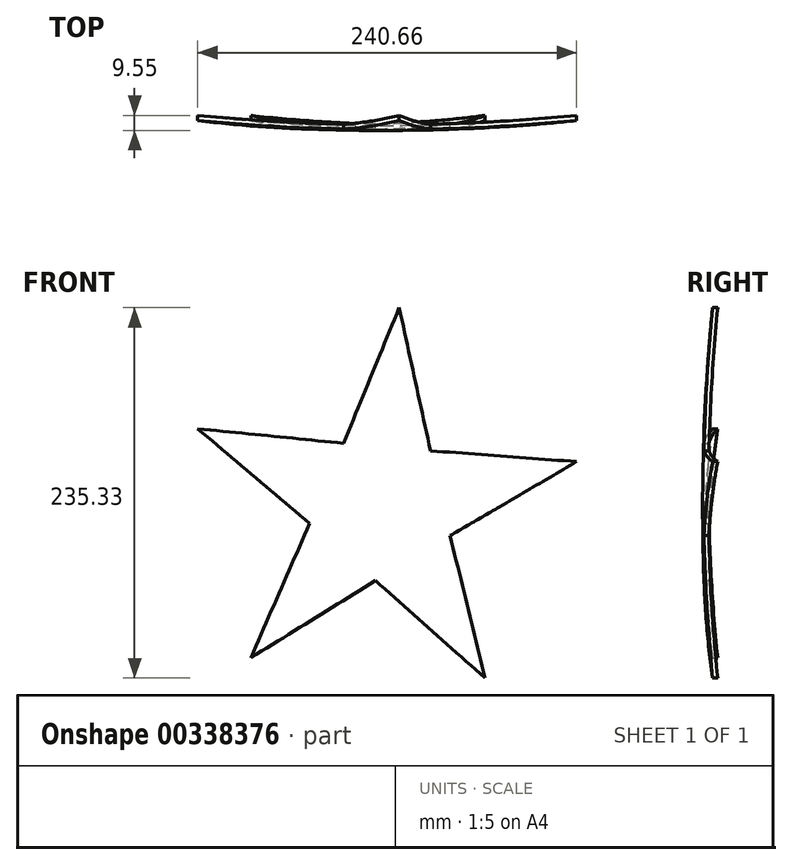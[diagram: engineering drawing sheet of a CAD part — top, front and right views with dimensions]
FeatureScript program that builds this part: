
annotation { "Feature Type Name" : "Feature", "Feature Type Description" : "" }
export const myFeature = defineFeature(function(context is Context, id is Id, definition is map)
    precondition{}
    {
        {
            var Q0;
            Q0=qCreatedBy(makeId("Top.planeOp"),FACE);
            var sketch = newSketch(context, id + "F0", { "sketchPlane" : qUnion([Q0])});
            skCircle(sketch, "E0", {"center": v(0, 986.65) * mm, "radius": 1270 * mm});
            skCircle(sketch, "E1", {"center": v(0, 986.65) * mm, "radius": 1263.65 * mm});
            skLineSegment(sketch, "E2", {"start": v(0, -277) * mm, "end": v(0, -283.35) * mm});
            skPoint(sketch, "E3", {"position": v(-508, -267.7) * mm});
            skLineSegment(sketch, "E4", {"start": v(-508, -267.7) * mm, "end": v(-508, -177.33) * mm});
            skLineSegment(sketch, "E5", {"start": v(-508, -177.33) * mm, "end": v(508, -177.33) * mm});
            skPoint(sketch, "E6", {"position": v(-177.8, -515.61) * mm});
            skPoint(sketch, "E7", {"position": v(-403.32, -498.82) * mm});
            skPoint(sketch, "E8", {"position": v(254, -269.6) * mm});
            skPoint(sketch, "E9", {"position": v(381, -241.86) * mm});
            skPoint(sketch, "E10.start.orphan", {"position": v(0, -280.18) * mm});
            skCircle(sketch, "E11", {"center": v(0, 986.65) * mm, "radius": 1266.83 * mm});
            skPoint(sketch, "E12.start.orphan", {"position": v(127, -280.18) * mm});
            skLineSegment(sketch, "E13", {"start": v(381, -241.86) * mm, "end": v(381, -221.53) * mm});
            skLineSegment(sketch, "E14", {"start": v(254, -269.6) * mm, "end": v(254, -254.45) * mm});
            skLineSegment(sketch, "E15", {"start": v(127, -280.18) * mm, "end": v(127, -273.8) * mm});
            skSolve(sketch);
        }
        {
            var Q0;
            {var subQ0=sQuery(id+"F0.wireOp",EDGE,"E2");var subQ1=sQuery(id+"F0.wireOp",EDGE,"E0");var subQ2=makeQuery(id+"F0.imprint","INTERSECT",VERTEX,{"derivedFrom":[subQ1,subQ0]});Q0=makeQuery(id+"F0.imprint","IMPRINT",FACE,{"disambiguationData":[TD([[makeQuery(id+"F0.imprint","IMPRINT",EDGE,{"disambiguationData":[TD([[subQ2,-1.0]])],"derivedFrom":subQ1}),1.0]])]});}
            var Q1;
            Q1=sQuery(id+"F0.wireOp",EDGE,"E2");
            revolve(context, id + "F1", {"entities" : qUnion([Q0]), "axis" : qUnion([Q1]), "revolveType" : RevolveType.FULL});
        }
        {
            var Q0;
            Q0=qCreatedBy(makeId("Front.planeOp"),FACE);
            var sketch = newSketch(context, id + "F2", { "sketchPlane" : qUnion([Q0])});
            skPoint(sketch, "E16", {"position": v(0, 0) * mm});
            skCircle(sketch, "E17", {"center": v(0, 0) * mm, "radius": 127 * mm});
            skCircle(sketch, "E18.cCircle", {"center": v(0, 0) * mm, "radius": 38.1 * mm, "construction": true});
            skLineSegment(sketch, "E18.0", {"start": v(-45.88, -10.63) * mm, "end": v(-24.28, 40.35) * mm});
            skLineSegment(sketch, "E18.1", {"start": v(-24.28, 40.35) * mm, "end": v(30.87, 35.56) * mm});
            skLineSegment(sketch, "E18.2", {"start": v(30.87, 35.56) * mm, "end": v(43.36, -18.37) * mm});
            skLineSegment(sketch, "E18.3", {"start": v(43.36, -18.37) * mm, "end": v(-4.07, -46.92) * mm});
            skLineSegment(sketch, "E18.4", {"start": v(-4.07, -46.92) * mm, "end": v(-45.88, -10.63) * mm});
            skPoint(sketch, "E18.0.midPoint", {"position": v(-35.08, 14.86) * mm});
            skLineSegment(sketch, "E19", {"start": v(-24.98, -28.77) * mm, "end": v(-83.25, -95.9) * mm});
            skLineSegment(sketch, "E20", {"start": v(-83.25, -95.9) * mm, "end": v(-45.88, -10.63) * mm});
            skLineSegment(sketch, "E21", {"start": v(-4.07, -46.92) * mm, "end": v(-83.25, -95.9) * mm});
            skLineSegment(sketch, "E22", {"start": v(19.65, -32.64) * mm, "end": v(65.49, -108.81) * mm});
            skLineSegment(sketch, "E23", {"start": v(65.49, -108.81) * mm, "end": v(43.36, -18.37) * mm});
            skLineSegment(sketch, "E24", {"start": v(-4.07, -46.92) * mm, "end": v(65.49, -108.81) * mm});
            skLineSegment(sketch, "E25", {"start": v(-35.08, 14.86) * mm, "end": v(-116.94, 49.54) * mm});
            skLineSegment(sketch, "E26", {"start": v(-116.94, 49.54) * mm, "end": v(-45.88, -10.63) * mm});
            skLineSegment(sketch, "E27", {"start": v(-24.28, 40.35) * mm, "end": v(-116.94, 49.54) * mm});
            skLineSegment(sketch, "E28", {"start": v(37.12, 8.6) * mm, "end": v(123.72, 28.66) * mm});
            skLineSegment(sketch, "E29", {"start": v(123.72, 28.66) * mm, "end": v(30.87, 35.56) * mm});
            skLineSegment(sketch, "E30", {"start": v(43.36, -18.37) * mm, "end": v(123.72, 28.66) * mm});
            skLineSegment(sketch, "E31", {"start": v(3.3, 37.96) * mm, "end": v(10.98, 126.52) * mm});
            skLineSegment(sketch, "E32", {"start": v(10.98, 126.52) * mm, "end": v(-24.28, 40.35) * mm});
            skLineSegment(sketch, "E33", {"start": v(30.87, 35.56) * mm, "end": v(10.98, 126.52) * mm});
            skSolve(sketch);
        }
        {
            var Q0;
            {var subQ0=sQuery(id+"F2.wireOp",EDGE,"E20");Q0=makeQuery(id+"F2.imprint","IMPRINT",FACE,{"disambiguationData":[TD([[makeQuery(id+"F2.imprint","IMPRINT",EDGE,{"derivedFrom":subQ0}),1.0]])]});}
            var Q1;
            {var subQ0=sQuery(id+"F2.wireOp",EDGE,"E21");Q1=makeQuery(id+"F2.imprint","IMPRINT",FACE,{"disambiguationData":[TD([[makeQuery(id+"F2.imprint","IMPRINT",EDGE,{"derivedFrom":subQ0}),1.0]])]});}
            var Q2;
            {var subQ0=sQuery(id+"F2.wireOp",EDGE,"E23");Q2=makeQuery(id+"F2.imprint","IMPRINT",FACE,{"disambiguationData":[TD([[makeQuery(id+"F2.imprint","IMPRINT",EDGE,{"derivedFrom":subQ0}),-1.0]])]});}
            var Q3;
            {var subQ0=sQuery(id+"F2.wireOp",EDGE,"E29");Q3=makeQuery(id+"F2.imprint","IMPRINT",FACE,{"disambiguationData":[TD([[makeQuery(id+"F2.imprint","IMPRINT",EDGE,{"derivedFrom":subQ0}),-1.0]])]});}
            var Q4;
            {var subQ0=sQuery(id+"F2.wireOp",EDGE,"E27");Q4=makeQuery(id+"F2.imprint","IMPRINT",FACE,{"disambiguationData":[TD([[makeQuery(id+"F2.imprint","IMPRINT",EDGE,{"derivedFrom":subQ0}),-1.0]])]});}
            extrude(context, id + "F3", {"entities" : qUnion([Q0, Q1, Q2, Q3, Q4]), "operationType" : NewBodyOperationType.REMOVE, "endBound" : BoundingType.THROUGH_ALL, "depth" : 25.4 * mm});
        }
        {
            var Q0;
            Q0=qCreatedBy(makeId("Front.planeOp"),FACE);
            cPlane(context, id + "F4", {"entities" : qUnion([Q0]), "cplaneType" : CPlaneType.OFFSET, "offset" : 307.34 * mm, "width" : 152.4 * mm, "height" : 152.4 * mm});
        }
    });
